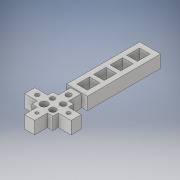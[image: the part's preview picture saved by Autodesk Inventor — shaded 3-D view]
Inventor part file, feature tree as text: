
AUTODESK INVENTOR PART (.ipt)
format: ipt  version: 2019 (Build 230136000, 136)  size: 194,048 bytes
history: native  units: mm
features: extrude x1, sketch x1
ambient origin geometry x8: Origin, YZ Plane, XZ Plane, XY Plane, X Axis, Y Axis, Z Axis, Center Point
bodies: Solid1 (feature_tree)
feature tree (2):
  extrude  "Extrusion1"  Depth=10.0mm
  sketch  "Sketch1"  dims[d0=10.0mm d1=10.0mm d2=10.0mm d3=35.0mm d4=5.0mm d5=6.0mm d6=2.5mm d7=2.5mm d8=6.5mm d9=5.0mm d10=6.0mm d11=6.05mm d12=4.95mm d13=4.9mm d14=6.1mm d15=6.15mm d16=4.85mm d17=2.5mm d18=2.5mm d19=1.5mm d20=1.8mm d21=2.0mm d22=2.5mm d23=3.0mm d24=3.5mm d25=2.25mm d26=2.75mm d27=2.5mm d28=2.5mm d29=2.5mm d30=2.5mm d31=2.5mm d32=2.5mm d33=2.4mm d34=2.5mm d35=2.8mm d36=2.5mm d37=2.6mm d38=2.6mm d39=2.6mm d40=2.9mm d41=2.9mm d42=2.6mm d43=6.0mm d44=0.0mm d45=5.0mm d46=5.95mm d47=5.0mm d48=5.9mm d49=2.0mm d50=2.0mm d51=2.0mm d52=6.05mm]
